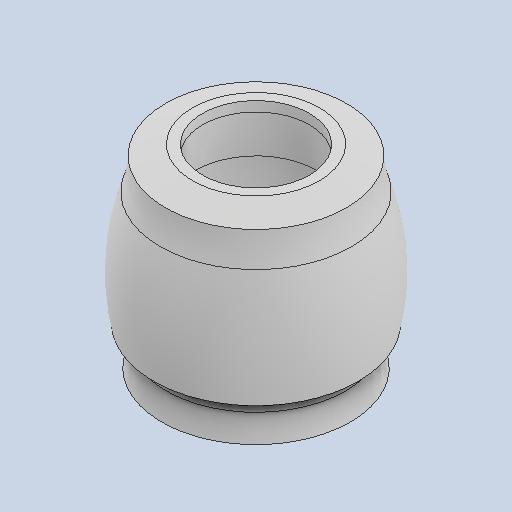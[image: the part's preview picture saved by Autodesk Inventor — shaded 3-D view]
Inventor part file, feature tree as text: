
AUTODESK INVENTOR PART (.ipt)
format: ipt  version: 2022 (Build 260153000, 153)  size: 172,544 bytes
history: native  units: in
note: dims shown in document units (in); Inventor stores cm internally (conversion verified against a paired STEP export)
features: revolve x1
ambient origin geometry x8: Origin, YZ Plane, XZ Plane, XY Plane, X Axis, Y Axis, Z Axis, Center Point
bodies: Solid1 (feature_tree)
feature tree (1):
  revolve  "Revolve1"  [1 undecoded]
note: 1 required parameter value undecoded (feature->parameter linkage not recoverable at this tier; creation-order binding heuristic only, values carry confidence <= 0.55)
